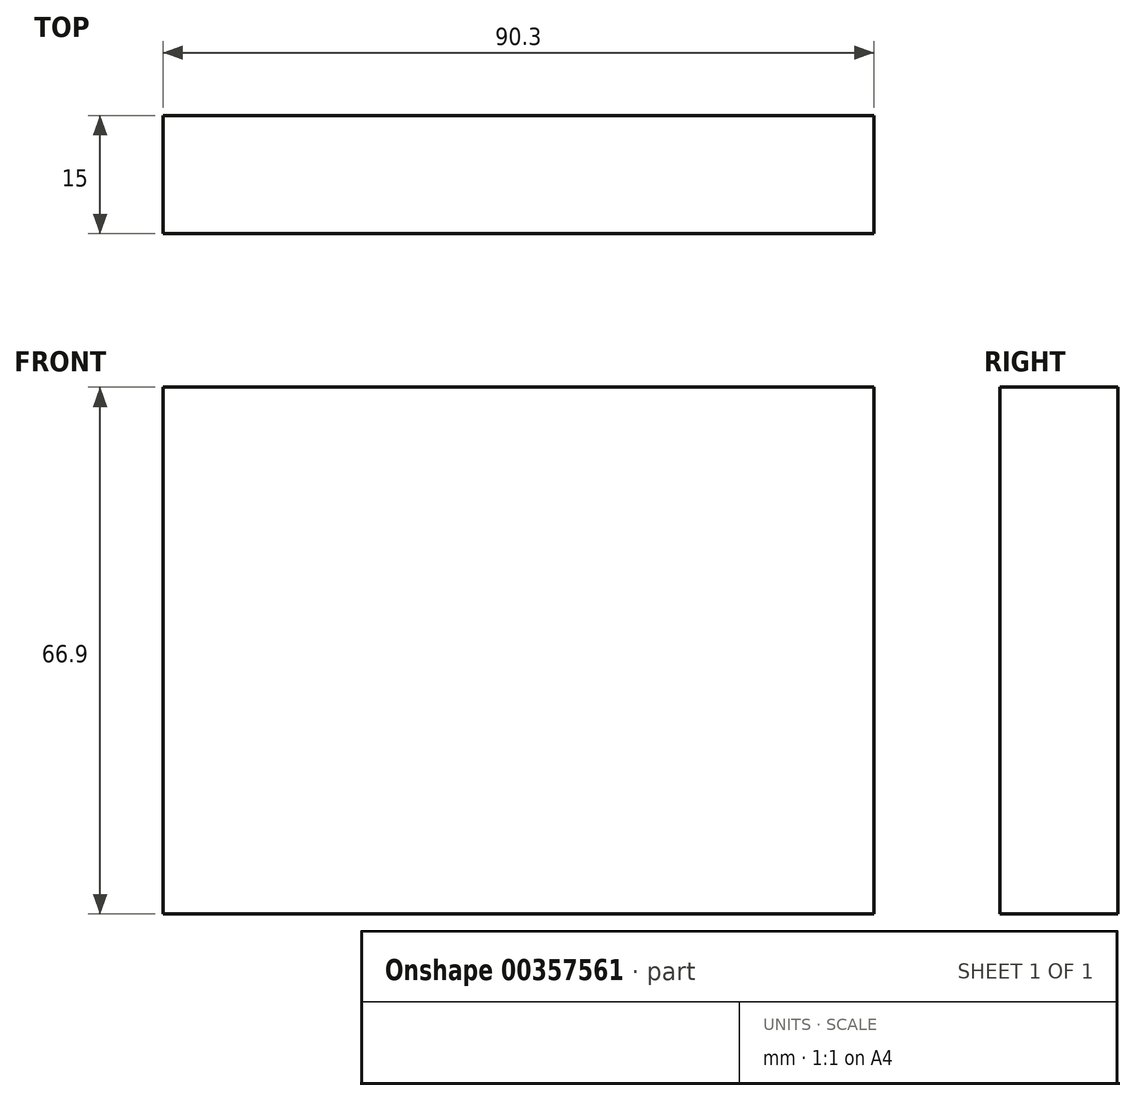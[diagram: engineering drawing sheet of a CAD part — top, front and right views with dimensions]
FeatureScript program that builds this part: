
annotation { "Feature Type Name" : "Feature", "Feature Type Description" : "" }
export const myFeature = defineFeature(function(context is Context, id is Id, definition is map)
    precondition{}
    {
        {
            var Q0;
            Q0=qCreatedBy(makeId("Front.planeOp"),FACE);
            var sketch = newSketch(context, id + "F0", { "sketchPlane" : qUnion([Q0])});
            skLineSegment(sketch, "E0.bottom", {"start": v(45.15, 33.45) * mm, "end": v(-45.15, 33.45) * mm});
            skLineSegment(sketch, "E0.top", {"start": v(45.15, -33.45) * mm, "end": v(-45.15, -33.45) * mm});
            skLineSegment(sketch, "E0.left", {"start": v(45.15, 33.45) * mm, "end": v(45.15, -33.45) * mm});
            skLineSegment(sketch, "E0.right", {"start": v(-45.15, 33.45) * mm, "end": v(-45.15, -33.45) * mm});
            skPoint(sketch, "E0.middle", {"position": v(0, 0) * mm});
            skSolve(sketch);
        }
        {
            var Q0;
            Q0=makeQuery(id+"F0.imprint","IMPRINT",FACE,{"disambiguationData":[TD([[makeQuery(id+"F0.imprint","IMPRINT",EDGE,{"derivedFrom":sQuery(id+"F0.wireOp",EDGE,"E0.bottom")}),1.0]])]});
            extrude(context, id + "F1", {"entities" : qUnion([Q0]), "endBound" : BoundingType.SYMMETRIC, "depth" : 15 * mm});
        }
    });
